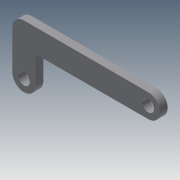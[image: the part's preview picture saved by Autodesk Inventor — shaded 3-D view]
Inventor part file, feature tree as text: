
AUTODESK INVENTOR PART (.ipt)
format: ipt  version: 2013 (Build 170138000, 138)  size: 100,352 bytes
history: native  units: mm
features: extrude x2, sketch x2
ambient origin geometry x8: Origin, YZ Plane, XZ Plane, XY Plane, X Axis, Y Axis, Z Axis, Center Point
bodies: Solid1 (feature_tree)
feature tree (4):
  extrude  "Extrusion1"  Depth=6.0mm
  extrude  "Extrusion2"  Depth=6.0mm
  sketch  "Sketch1"  dims[d0=32.0mm d1=6.0mm]
  sketch  "Sketch2"  dims[d2=6.0mm d3=6.0mm d4=10.0mm d5=6.0mm d6=2.0mm d7=0.0mm d8=3.0mm d9=3.0mm d10=2.0mm d11=0.0mm]
